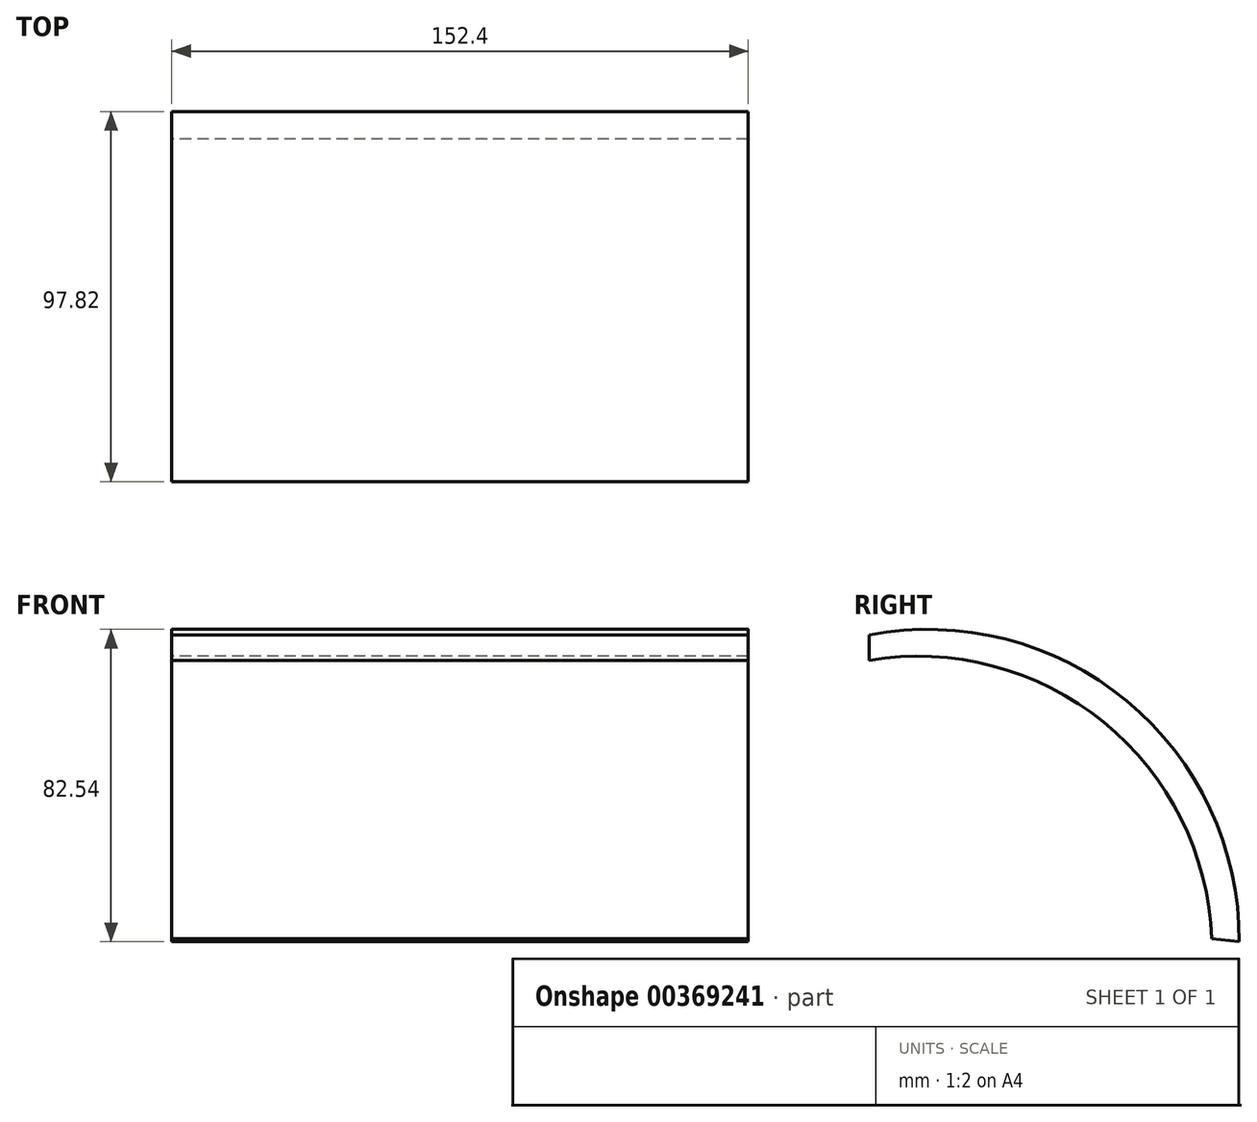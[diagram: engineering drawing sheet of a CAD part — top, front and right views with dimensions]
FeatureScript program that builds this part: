
annotation { "Feature Type Name" : "Feature", "Feature Type Description" : "" }
export const myFeature = defineFeature(function(context is Context, id is Id, definition is map)
    precondition{}
    {
        {
            var Q0;
            Q0=qCreatedBy(makeId("Right.planeOp"),FACE);
            var sketch = newSketch(context, id + "F0", { "sketchPlane" : qUnion([Q0])});
            skArc(sketch, "E0", {"start": v(47.49, -25.8) * mm, "mid": v(17.73, 37.83) * mm, "end": v(-50.33, 55.23) * mm});
            skArc(sketch, "E1", {"start": v(40.26, -25.04) * mm, "mid": v(11.6, 32.22) * mm, "end": v(-50.33, 48.52) * mm});
            skLineSegment(sketch, "E2", {"start": v(-50.33, 55.23) * mm, "end": v(-50.33, 48.52) * mm});
            skLineSegment(sketch, "E3", {"start": v(40.26, -25.04) * mm, "end": v(47.49, -25.8) * mm});
            skSolve(sketch);
        }
        {
            var Q0;
            Q0 = qSketchRegion(id + "F0", true);
            extrude(context, id + "F1", {"entities" : qUnion([Q0]), "depth" : 152.4 * mm});
        }
    });
